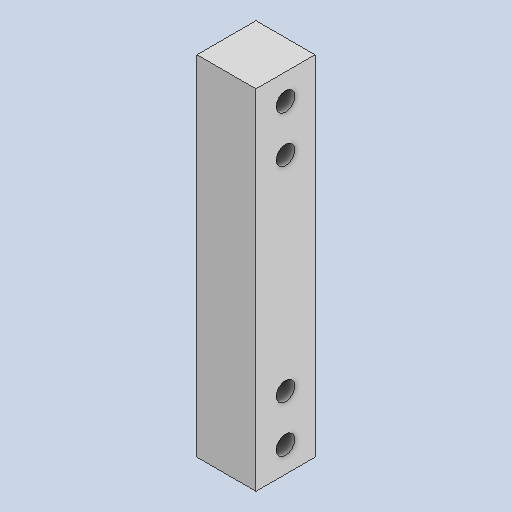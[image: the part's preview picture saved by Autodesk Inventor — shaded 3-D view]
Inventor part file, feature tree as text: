
AUTODESK INVENTOR PART (.ipt)
format: ipt  version: 2022 (Build 260153000, 153)  size: 94,720 bytes
history: native  units: in
note: dims shown in document units (in); Inventor stores cm internally (conversion verified against a paired STEP export)
features: other x3, sketch x2
ambient origin geometry x8: Origin, YZ Plane, XZ Plane, XY Plane, X Axis, Y Axis, Z Axis, Center Point
bodies: Solid1 (feature_tree)
feature tree (5):
  other  "Load_Cell.ipt"
  other  "Solid1::Load_Cell.ipt"
  other  "TaggingFeature1"
  sketch  "Sketch2"  dims[d0=0.3937in]
  sketch  "Sketch3"
